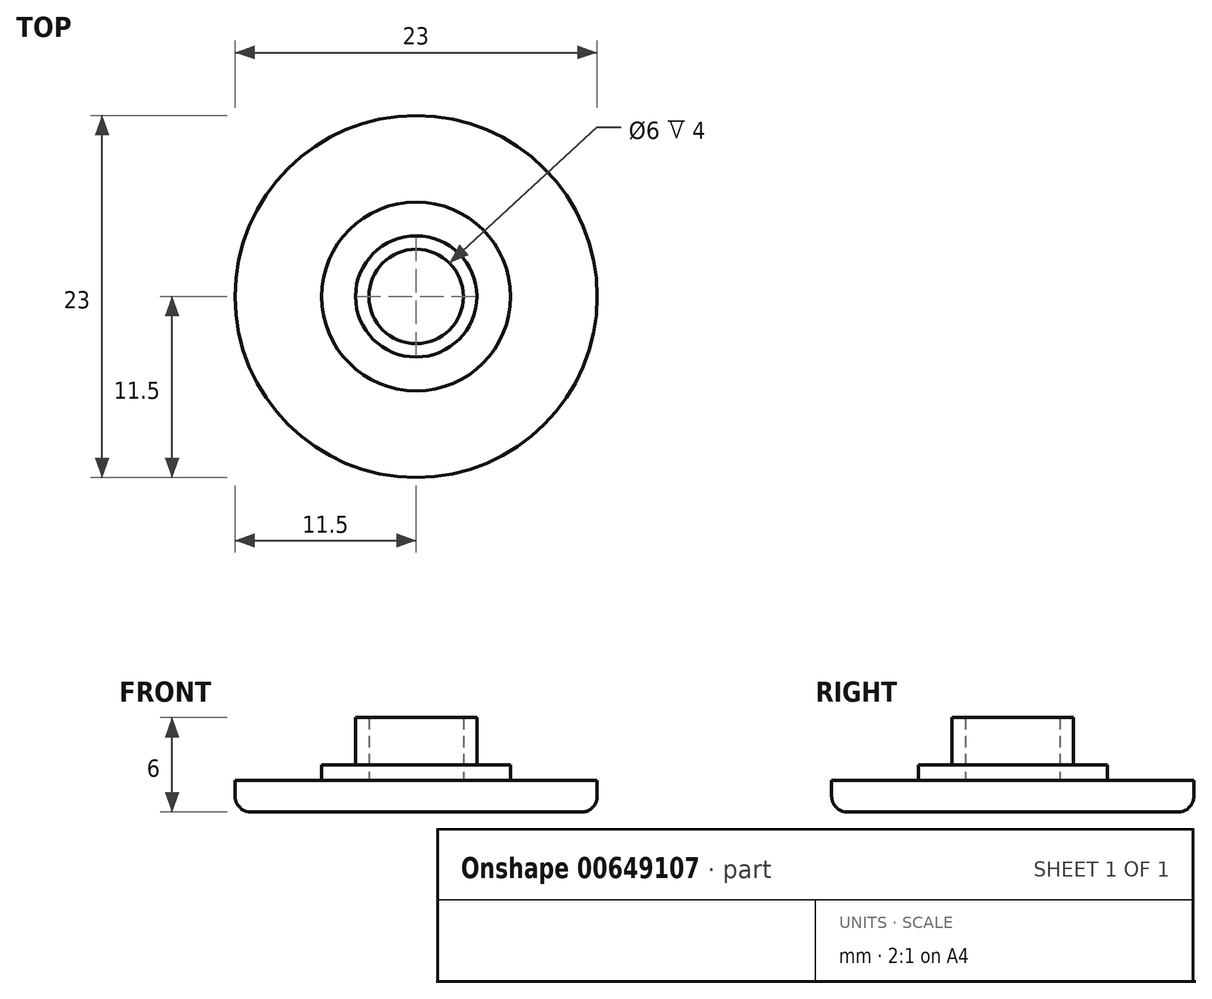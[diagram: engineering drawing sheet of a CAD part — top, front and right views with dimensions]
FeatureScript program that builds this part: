
annotation { "Feature Type Name" : "Feature", "Feature Type Description" : "" }
export const myFeature = defineFeature(function(context is Context, id is Id, definition is map)
    precondition{}
    {
        {
            var Q0;
            Q0=qCreatedBy(makeId("Top.planeOp"),FACE);
            var sketch = newSketch(context, id + "F0", { "sketchPlane" : qUnion([Q0])});
            skCircle(sketch, "E0", {"center": v(0, 0) * mm, "radius": 11.5 * mm});
            skSolve(sketch);
        }
        {
            var Q0;
            Q0=makeQuery(id+"F0.imprint","IMPRINT",FACE,{"disambiguationData":[TD([[makeQuery(id+"F0.imprint","IMPRINT",EDGE,{"derivedFrom":sQuery(id+"F0.wireOp",EDGE,"E0")}),1.0]])]});
            extrude(context, id + "F1", {"entities" : qUnion([Q0]), "depth" : 2 * mm, "offsetDistance" : 25 * mm});
        }
        {
            var Q0;
            Q0=makeQuery(id+"F1.opExtrude","CAP_EDGE",EDGE,{"disambiguationData":[OSD([sQuery(id+"F0.wireOp",EDGE,"E0")])],"isStart":true});
            fillet(context, id + "F2", {"entities" : qUnion([Q0]), "radius" : 1 * mm, "tangentPropagation" : true, "allowEdgeOverflow" : false});
        }
        {
            var Q0;
            Q0=makeQuery(id+"F1.opExtrude","CAP_FACE",FACE,{"disambiguationData":[OSD([sQuery(id+"F0.wireOp",EDGE,"E0")])],"isStart":false});
            var sketch = newSketch(context, id + "F3", { "sketchPlane" : qUnion([Q0])});
            skCircle(sketch, "E1", {"center": v(0, 0) * mm, "radius": 3.85 * mm});
            skCircle(sketch, "E2", {"center": v(0, 0) * mm, "radius": 3 * mm});
            skCircle(sketch, "E3", {"center": v(0, 0) * mm, "radius": 6 * mm});
            skSolve(sketch);
        }
        {
            var Q0;
            Q0=makeQuery(id+"F3.imprint","IMPRINT",FACE,{"disambiguationData":[TD([[makeQuery(id+"F3.imprint","IMPRINT",EDGE,{"derivedFrom":sQuery(id+"F3.wireOp",EDGE,"E1")}),1.0]])]});
            extrude(context, id + "F4", {"entities" : qUnion([Q0]), "operationType" : NewBodyOperationType.ADD, "depth" : 4 * mm, "offsetDistance" : 25 * mm});
        }
        {
            var Q0;
            Q0=makeQuery(id+"F3.imprint","IMPRINT",FACE,{"disambiguationData":[TD([[makeQuery(id+"F3.imprint","IMPRINT",EDGE,{"derivedFrom":sQuery(id+"F3.wireOp",EDGE,"E1")}),-1.0]])]});
            extrude(context, id + "F5", {"entities" : qUnion([Q0]), "operationType" : NewBodyOperationType.ADD, "depth" : 1 * mm, "offsetDistance" : 25 * mm});
        }
    });
